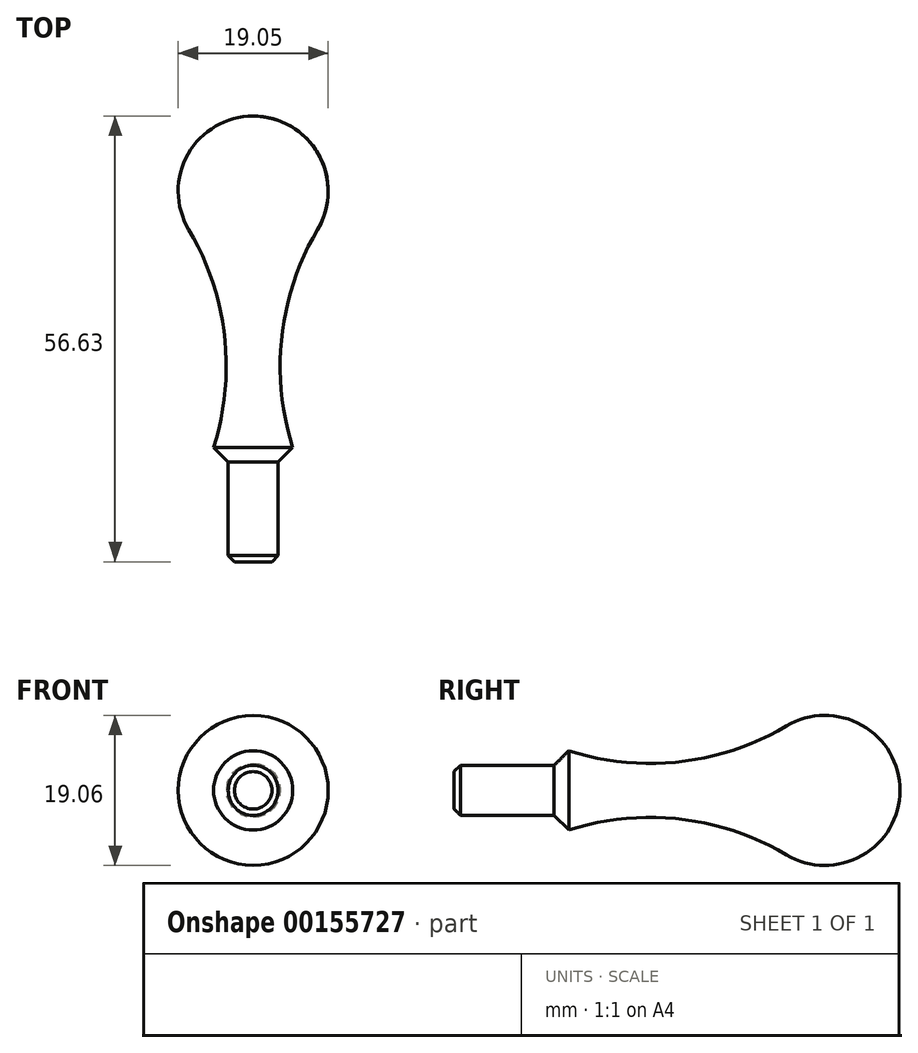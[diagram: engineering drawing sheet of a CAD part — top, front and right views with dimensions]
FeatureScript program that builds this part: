
annotation { "Feature Type Name" : "Feature", "Feature Type Description" : "" }
export const myFeature = defineFeature(function(context is Context, id is Id, definition is map)
    precondition{}
    {
        {
            var Q0;
            Q0=qCreatedBy(makeId("Top.planeOp"),FACE);
            var sketch = newSketch(context, id + "F0", { "sketchPlane" : qUnion([Q0])});
            skArc(sketch, "E0", {"start": v(8.2, 39.59) * mm, "mid": v(8.28, 49.16) * mm, "end": v(0, 53.98) * mm});
            skLineSegment(sketch, "E1", {"start": v(0, 53.98) * mm, "end": v(0, -2.65) * mm});
            skLineSegment(sketch, "E2", {"start": v(5.03, 11.9) * mm, "end": v(3.17, 10.05) * mm});
            skLineSegment(sketch, "E3", {"start": v(0, 0) * mm, "end": v(9.53, 0) * mm, "construction": true});
            skLineSegment(sketch, "E4", {"start": v(3.17, 10.05) * mm, "end": v(3.18, -2.65) * mm});
            skLineSegment(sketch, "E5", {"start": v(3.17, -2.65) * mm, "end": v(0, -2.65) * mm});
            skLineSegment(sketch, "E6", {"start": v(-8.2, 39.59) * mm, "end": v(8.2, 39.59) * mm, "construction": true});
            skArc(sketch, "E7", {"start": v(8.2, 39.59) * mm, "mid": v(3.65, 26.09) * mm, "end": v(5.03, 11.9) * mm});
            skSolve(sketch);
        }
        {
            var Q0;
            Q0 = qSketchRegion(id + "F0", true);
            var Q1;
            Q1=sQuery(id+"F0.wireOp",EDGE,"E1");
            revolve(context, id + "F1", {"entities" : qUnion([Q0]), "axis" : qUnion([Q1]), "revolveType" : RevolveType.FULL});
        }
        {
            var Q0;
            Q0=makeQuery(id+"F1.opRevolve","SWEPT_EDGE",EDGE,{"disambiguationData":[OSD([sQuery(id+"F0.wireOp",EDGE,"E4"),sQuery(id+"F0.wireOp",EDGE,"E5")])]});
            chamfer(context, id + "F2", {"entities" : qUnion([Q0]), "width" : 0.8 * mm, "tangentPropagation" : true});
        }
    });
